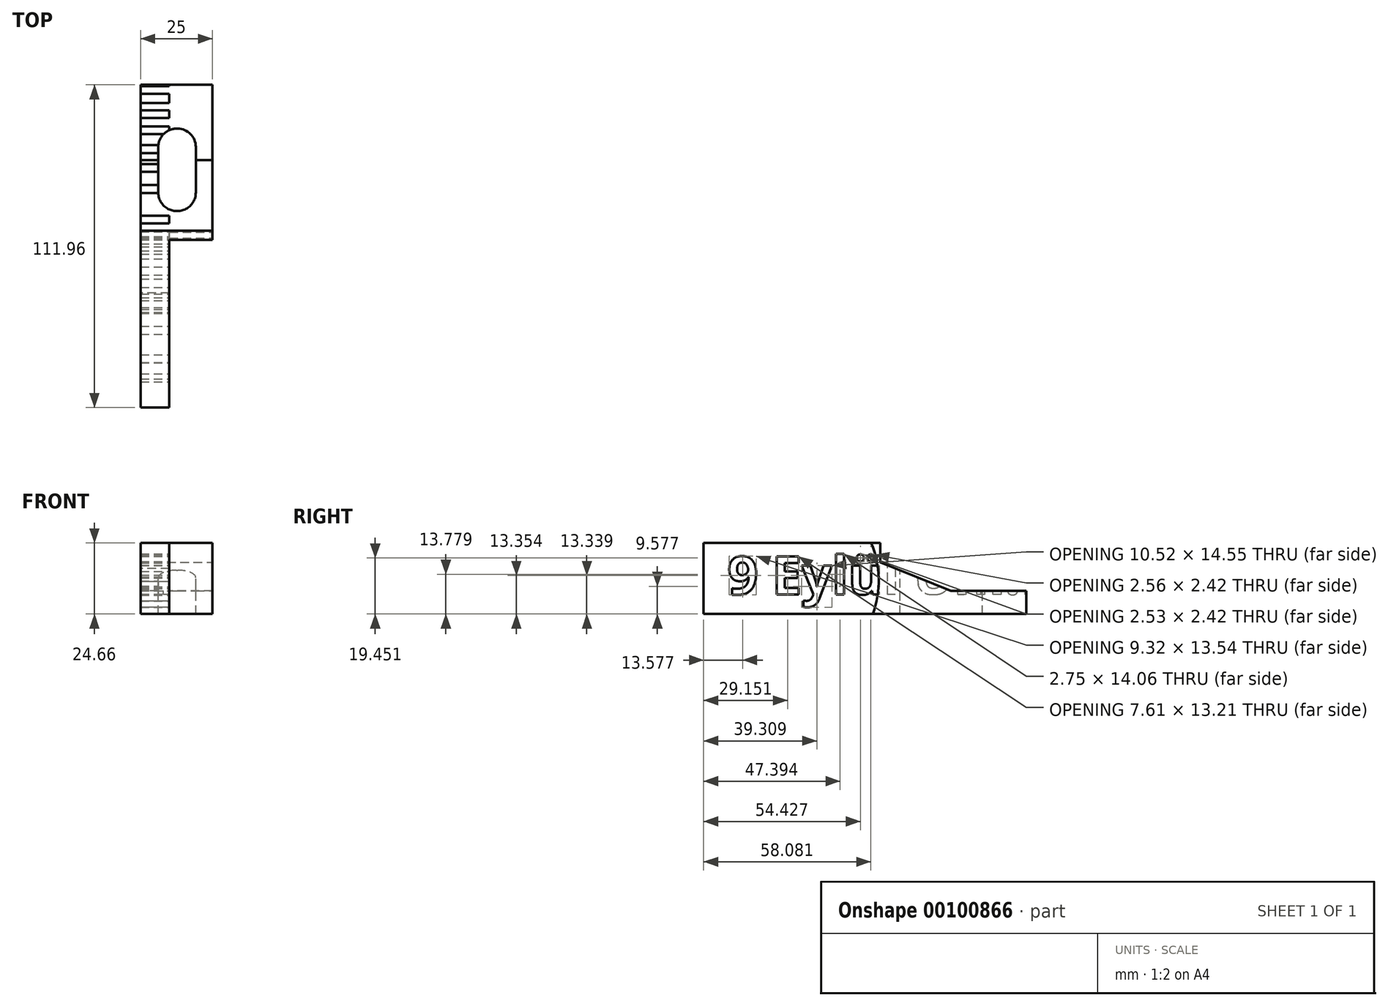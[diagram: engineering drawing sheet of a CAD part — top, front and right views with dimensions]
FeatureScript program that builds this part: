
annotation { "Feature Type Name" : "Feature", "Feature Type Description" : "" }
export const myFeature = defineFeature(function(context is Context, id is Id, definition is map)
    precondition{}
    {
        {
            var Q0;
            Q0=qCreatedBy(makeId("Right.planeOp"),FACE);
            var sketch = newSketch(context, id + "F0", { "sketchPlane" : qUnion([Q0])});
            skLineSegment(sketch, "E0.bottom", {"start": v(-55.98, -28.3) * mm, "end": v(55.98, -28.3) * mm});
            skLineSegment(sketch, "E0.top", {"start": v(-55.98, -52.96) * mm, "end": v(55.98, -52.96) * mm});
            skLineSegment(sketch, "E0.left", {"start": v(-55.98, -28.3) * mm, "end": v(-55.98, -52.96) * mm});
            skLineSegment(sketch, "E0.right", {"start": v(55.98, -28.3) * mm, "end": v(55.98, -52.96) * mm});
            skSolve(sketch);
        }
        {
            var Q0;
            Q0 = qSketchRegion(id + "F0", true);
            extrude(context, id + "F1", {"entities" : qUnion([Q0]), "depth" : 25 * mm});
        }
        {
            var Q0;
            Q0=makeQuery(id+"F1.opExtrude","SWEPT_FACE",FACE,{"disambiguationData":[OSD([sQuery(id+"F0.wireOp",EDGE,"E0.bottom")])]});
            var sketch = newSketch(context, id + "F6", { "sketchPlane" : qUnion([Q0])});
            skLineSegment(sketch, "E1.bottom", {"start": v(12.52, 40.78) * mm, "end": v(12.84, 40.78) * mm});
            skLineSegment(sketch, "E1.top", {"start": v(12.52, 12.2) * mm, "end": v(12.84, 12.2) * mm});
            skLineSegment(sketch, "E1.left", {"start": v(6.17, 34.43) * mm, "end": v(6.17, 18.55) * mm});
            skLineSegment(sketch, "E1.right", {"start": v(19.2, 34.43) * mm, "end": v(19.2, 18.55) * mm});
            skPoint(sketch, "E2.visualSharp", {"position": v(6.17, 12.2) * mm});
            skArc(sketch, "E2.filletArc", {"start": v(6.17, 18.55) * mm, "mid": v(8.03, 14.06) * mm, "end": v(12.52, 12.2) * mm});
            skPoint(sketch, "E3.visualSharp", {"position": v(19.2, 40.78) * mm});
            skArc(sketch, "E3.filletArc", {"start": v(19.2, 34.43) * mm, "mid": v(17.33, 38.92) * mm, "end": v(12.84, 40.78) * mm});
            skPoint(sketch, "E4.visualSharp", {"position": v(19.2, 12.2) * mm});
            skArc(sketch, "E4.filletArc", {"start": v(12.84, 12.2) * mm, "mid": v(17.33, 14.06) * mm, "end": v(19.2, 18.55) * mm});
            skPoint(sketch, "E5.visualSharp", {"position": v(6.17, 40.78) * mm});
            skArc(sketch, "E5.filletArc", {"start": v(12.52, 40.78) * mm, "mid": v(8.03, 38.92) * mm, "end": v(6.17, 34.43) * mm});
            skSolve(sketch);
        }
        {
            var Q0;
            Q0 = qSketchRegion(id + "F6", true);
            extrude(context, id + "F2", {"entities" : qUnion([Q0]), "operationType" : NewBodyOperationType.REMOVE, "oppositeDirection" : true, "depth" : 25 * mm});
        }
        {
            var Q0;
            Q0=makeQuery(id+"F1.opExtrude","CAP_FACE",FACE,{"disambiguationData":[OSD([sQuery(id+"F0.wireOp",EDGE,"E0.bottom"),sQuery(id+"F0.wireOp",EDGE,"E0.top"),sQuery(id+"F0.wireOp",EDGE,"E0.left"),sQuery(id+"F0.wireOp",EDGE,"E0.right")])],"isStart":false});
            var sketch = newSketch(context, id + "F7", { "sketchPlane" : qUnion([Q0])});
            skLineSegment(sketch, "E6", {"start": v(5.37, -23.55) * mm, "end": v(5.37, -35) * mm});
            skLineSegment(sketch, "E7", {"start": v(5.37, -35) * mm, "end": v(29.9, -44.98) * mm});
            skLineSegment(sketch, "E8", {"start": v(29.9, -44.98) * mm, "end": v(65.5, -44.98) * mm});
            skLineSegment(sketch, "E9", {"start": v(65.5, -44.98) * mm, "end": v(65.5, -23.55) * mm});
            skLineSegment(sketch, "E10", {"start": v(65.5, -23.55) * mm, "end": v(6.79, -23.56) * mm});
            skLineSegment(sketch, "E11", {"start": v(5.37, -23.55) * mm, "end": v(6.79, -23.56) * mm});
            skSolve(sketch);
        }
        {
            var Q0;
            Q0 = qSketchRegion(id + "F7", true);
            extrude(context, id + "F3", {"entities" : qUnion([Q0]), "operationType" : NewBodyOperationType.REMOVE, "oppositeDirection" : true, "depth" : 25 * mm});
        }
        {
            var Q0;
            Q0=makeQuery(id+"F1.opExtrude","CAP_FACE",FACE,{"disambiguationData":[OSD([sQuery(id+"F0.wireOp",EDGE,"E0.bottom"),sQuery(id+"F0.wireOp",EDGE,"E0.top"),sQuery(id+"F0.wireOp",EDGE,"E0.left"),sQuery(id+"F0.wireOp",EDGE,"E0.right")])],"isStart":false});
            var sketch = newSketch(context, id + "F4", { "sketchPlane" : qUnion([Q0])});
            skCircle(sketch, "E12", {"center": v(-29, -41.36) * mm, "radius": 33.8 * mm});
            skSolve(sketch);
        }
        {
            var Q0;
            Q0 = qSketchRegion(id + "F4", true);
            extrude(context, id + "F5", {"entities" : qUnion([Q0]), "operationType" : NewBodyOperationType.REMOVE, "oppositeDirection" : true, "depth" : 15 * mm});
        }
        {
            var Q0;
            Q0=makeQuery(id+"F5.boolean.opBoolean","COPY",FACE,{"derivedFrom":makeQuery(id+"F5.opExtrude","CAP_FACE",FACE,{"disambiguationData":[OSD([sQuery(id+"F4.wireOp",EDGE,"E12")])],"isStart":false})});
            var sketch = newSketch(context, id + "F8", { "sketchPlane" : qUnion([Q0])});
            skText(sketch, "E13", { "text": "9 Eylül Üni.Mechanical Enginering", "fontName": "OpenSans-Bold.ttf"});
            const initialGuessFlswZcFgLOOhMkyyF_1  = {"E13": [-0.04766, -0.04621, 1, 0, 0.01332]};
            skSetInitialGuess(sketch, initialGuessFlswZcFgLOOhMkyyF_1);
            skSolve(sketch);
        }
        {
            var Q0;
            Q0 = qSketchRegion(id + "F8", true);
            extrude(context, id + "F9", {"entities" : qUnion([Q0]), "operationType" : NewBodyOperationType.REMOVE, "oppositeDirection" : true, "depth" : 10 * mm});
        }
    });
